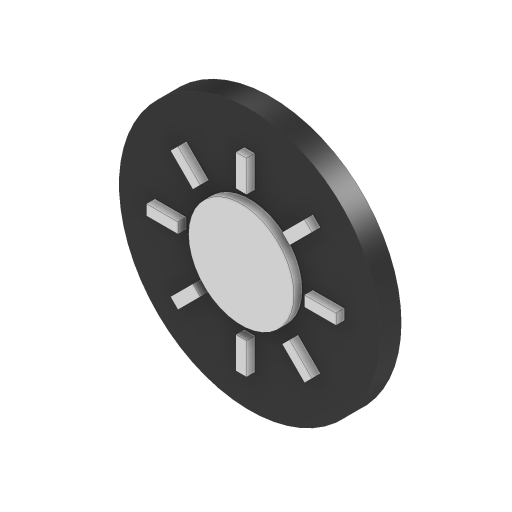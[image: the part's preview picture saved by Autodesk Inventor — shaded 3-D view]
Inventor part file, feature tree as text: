
AUTODESK INVENTOR PART (.ipt)
format: ipt  version: 2023 (Build 270158000, 158)  size: 295,936 bytes
history: native  units: mm
features: extrude x2, sketch x2, other x1
ambient origin geometry x8: Origin, YZ Plane, XZ Plane, XY Plane, X Axis, Y Axis, Z Axis, Center Point
bodies: Body1 (feature_tree)
feature tree (5):
  other  "Těleso1"
  extrude  "Vysunutí1"  Depth=12.4mm
  extrude  "Vysunutí2"  Depth=1.0mm TaperAngle=0.0deg
  sketch  "Náčrt1"
  sketch  "Náčrt2"
